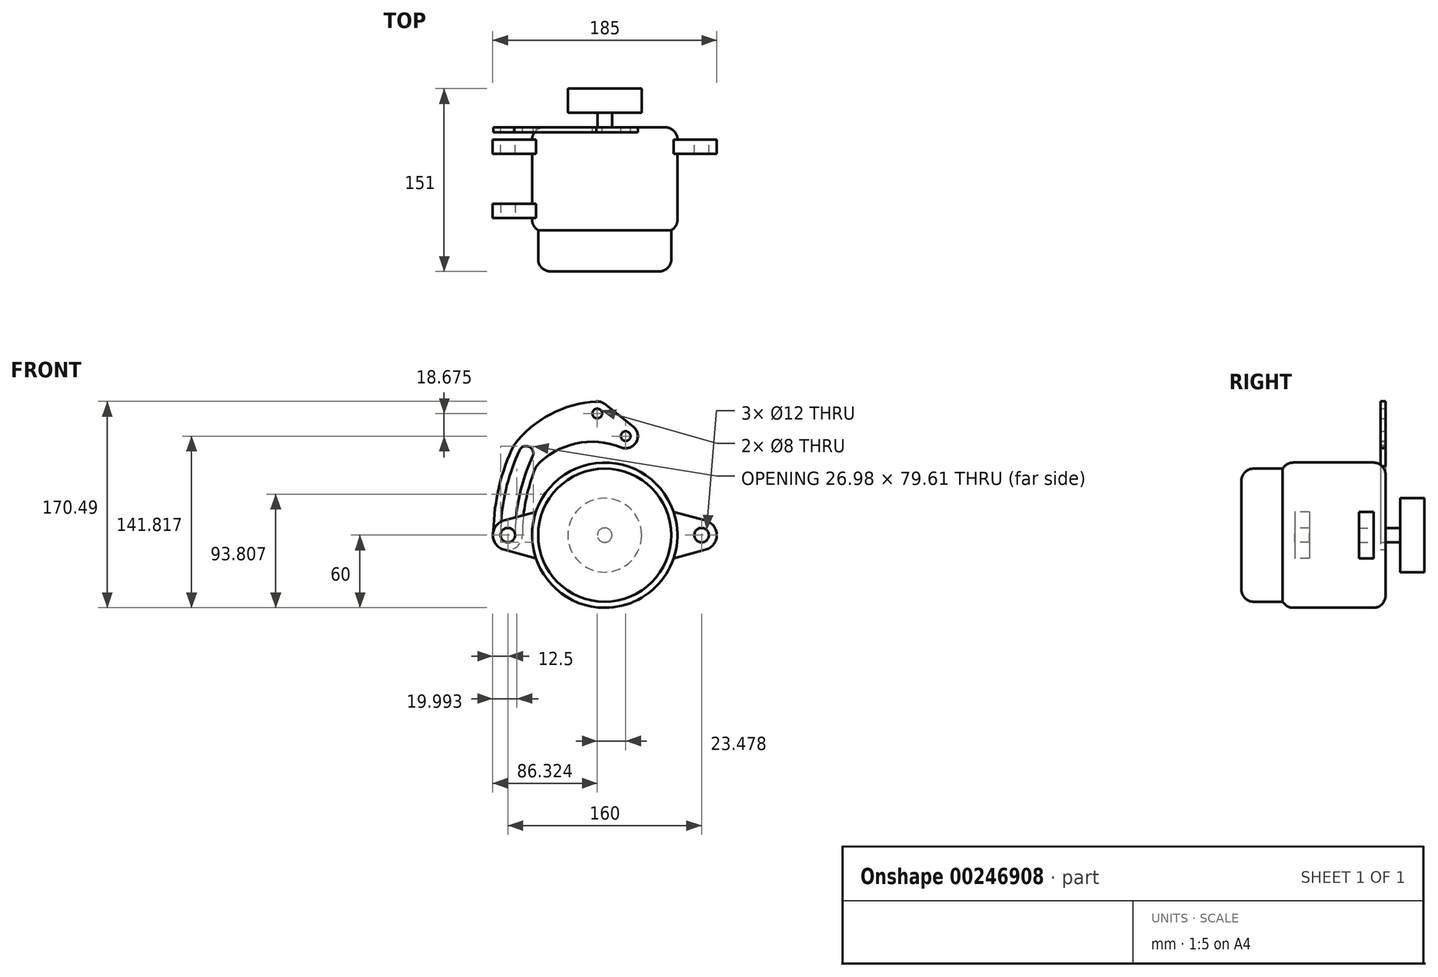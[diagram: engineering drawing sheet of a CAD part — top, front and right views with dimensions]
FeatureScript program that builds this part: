
annotation { "Feature Type Name" : "Feature", "Feature Type Description" : "" }
export const myFeature = defineFeature(function(context is Context, id is Id, definition is map)
    precondition{}
    {
        {
            var Q0;
            Q0=qCreatedBy(makeId("Front.planeOp"),FACE);
            var sketch = newSketch(context, id + "F0", { "sketchPlane" : qUnion([Q0])});
            skCircle(sketch, "E0", {"center": v(0, 0) * mm, "radius": 60 * mm});
            skSolve(sketch);
        }
        {
            var Q0;
            Q0=makeQuery(id+"F0.imprint","IMPRINT",FACE,{"disambiguationData":[TD([[makeQuery(id+"F0.imprint","IMPRINT",EDGE,{"derivedFrom":sQuery(id+"F0.wireOp",EDGE,"E0")}),1.0]])]});
            extrude(context, id + "F1", {"entities" : qUnion([Q0]), "depth" : 85 * mm});
        }
        {
            var Q0;
            Q0=makeQuery(id+"F1.opExtrude","CAP_FACE",FACE,{"disambiguationData":[OSD([sQuery(id+"F0.wireOp",EDGE,"E0")])],"isStart":false});
            var sketch = newSketch(context, id + "F2", { "sketchPlane" : qUnion([Q0])});
            skCircle(sketch, "E1", {"center": v(0, 0) * mm, "radius": 55 * mm});
            skSolve(sketch);
        }
        {
            var Q0;
            Q0 = qSketchRegion(id + "F2", true);
            extrude(context, id + "F3", {"entities" : qUnion([Q0]), "operationType" : NewBodyOperationType.ADD, "depth" : 34 * mm});
        }
        {
            var Q0;
            Q0=makeQuery(id+"F1.opExtrude","CAP_EDGE",EDGE,{"disambiguationData":[OSD([sQuery(id+"F0.wireOp",EDGE,"E0")])],"isStart":true});
            var Q1;
            Q1=makeQuery(id+"F1.opExtrude","CAP_EDGE",EDGE,{"disambiguationData":[OSD([sQuery(id+"F0.wireOp",EDGE,"E0")])],"isStart":false});
            var Q2;
            Q2=makeQuery(id+"F3.opExtrude","CAP_EDGE",EDGE,{"disambiguationData":[OSD([sQuery(id+"F2.wireOp",EDGE,"E1")])],"isStart":false});
            fillet(context, id + "F4", {"entities" : qUnion([Q0, Q1, Q2]), "radius" : 10 * mm, "tangentPropagation" : true, "allowEdgeOverflow" : false});
        }
        {
            var Q0;
            Q0=makeQuery(id+"F1.opExtrude","CAP_FACE",FACE,{"disambiguationData":[OSD([sQuery(id+"F0.wireOp",EDGE,"E0")])],"isStart":true});
            var sketch = newSketch(context, id + "F5", { "sketchPlane" : qUnion([Q0])});
            skCircle(sketch, "E2", {"center": v(0, 0) * mm, "radius": 6 * mm});
            skSolve(sketch);
        }
        {
            var Q0;
            Q0 = qSketchRegion(id + "F5", true);
            extrude(context, id + "F6", {"entities" : qUnion([Q0]), "operationType" : NewBodyOperationType.ADD, "depth" : 12 * mm});
        }
        {
            var Q0;
            Q0=makeQuery(id+"F6.opExtrude","CAP_FACE",FACE,{"disambiguationData":[OSD([sQuery(id+"F5.wireOp",EDGE,"E2")])],"isStart":false});
            var sketch = newSketch(context, id + "F7", { "sketchPlane" : qUnion([Q0])});
            skCircle(sketch, "E3", {"center": v(0, 0) * mm, "radius": 30.5 * mm});
            skSolve(sketch);
        }
        {
            var Q0;
            Q0 = qSketchRegion(id + "F7", true);
            extrude(context, id + "F8", {"entities" : qUnion([Q0]), "operationType" : NewBodyOperationType.ADD, "depth" : 20 * mm});
        }
        {
            var Q0;
            Q0=qCreatedBy(makeId("Front.planeOp"),FACE);
            cPlane(context, id + "F9", {"entities" : qUnion([Q0]), "cplaneType" : CPlaneType.OFFSET, "offset" : 10 * mm, "width" : 150 * mm, "height" : 150 * mm});
        }
        {
            var Q0;
            Q0=qCreatedBy(id+"F9.planeOp",FACE);
            var sketch = newSketch(context, id + "F10", { "sketchPlane" : qUnion([Q0])});
            skCircle(sketch, "E4", {"center": v(-80, 0) * mm, "radius": 6 * mm});
            skCircle(sketch, "E5", {"center": v(80, 0) * mm, "radius": 6 * mm});
            skArc(sketch, "E6", {"start": v(83.24, -12.07) * mm, "mid": v(92.5, 0) * mm, "end": v(83.24, 12.07) * mm});
            skArc(sketch, "E7", {"start": v(-83.24, 12.07) * mm, "mid": v(-92.5, 0) * mm, "end": v(-83.24, -12.07) * mm});
            skLineSegment(sketch, "E8", {"start": v(-83.24, 12.07) * mm, "end": v(-56.87, 19.14) * mm});
            skLineSegment(sketch, "E9", {"start": v(-83.24, -12.07) * mm, "end": v(-56.87, -19.14) * mm});
            skLineSegment(sketch, "E10", {"start": v(83.24, 12.07) * mm, "end": v(56.87, 19.14) * mm});
            skLineSegment(sketch, "E11", {"start": v(83.24, -12.07) * mm, "end": v(56.87, -19.14) * mm});
            skArc(sketch, "E12.0", {"start": v(56.87, -19.14) * mm, "mid": v(60, 0) * mm, "end": v(56.87, 19.14) * mm});
            skArc(sketch, "E13.trimOffspring", {"start": v(-56.87, 19.14) * mm, "mid": v(-60, 0) * mm, "end": v(-56.87, -19.14) * mm});
            skSolve(sketch);
        }
        {
            var Q0;
            Q0 = qSketchRegion(id + "F10", true);
            extrude(context, id + "F11", {"entities" : qUnion([Q0]), "operationType" : NewBodyOperationType.ADD, "depth" : 12 * mm});
        }
        {
            var Q0;
            Q0=qCreatedBy(makeId("Front.planeOp"),FACE);
            cPlane(context, id + "F12", {"entities" : qUnion([Q0]), "cplaneType" : CPlaneType.OFFSET, "offset" : 75 * mm, "width" : 150 * mm, "height" : 150 * mm});
        }
        {
            var Q0;
            Q0=qCreatedBy(id+"F12.planeOp",FACE);
            var sketch = newSketch(context, id + "F13", { "sketchPlane" : qUnion([Q0])});
            skArc(sketch, "E14.0.0", {"start": v(-56.87, -19.14) * mm, "mid": v(-60, 0) * mm, "end": v(-56.87, 19.14) * mm});
            skLineSegment(sketch, "E14.0.1", {"start": v(-56.87, 19.14) * mm, "end": v(-83.24, 12.07) * mm});
            skArc(sketch, "E14.0.2", {"start": v(-83.24, 12.07) * mm, "mid": v(-92.5, 0) * mm, "end": v(-83.24, -12.07) * mm});
            skLineSegment(sketch, "E14.0.3", {"start": v(-83.24, -12.07) * mm, "end": v(-56.87, -19.14) * mm});
            skCircle(sketch, "E15.0", {"center": v(-80, 0) * mm, "radius": 6 * mm});
            skSolve(sketch);
        }
        {
            var Q0;
            Q0 = qSketchRegion(id + "F13", true);
            extrude(context, id + "F14", {"entities" : qUnion([Q0]), "operationType" : NewBodyOperationType.ADD, "oppositeDirection" : true, "depth" : 12 * mm});
        }
        {
            var Q0;
            Q0=qCreatedBy(makeId("Front.planeOp"),FACE);
            var sketch = newSketch(context, id + "F15", { "sketchPlane" : qUnion([Q0])});
            skCircle(sketch, "E16.0", {"center": v(80, 0) * mm, "radius": 6 * mm, "construction": true});
            skArc(sketch, "E17.1", {"start": v(-86, 0) * mm, "mid": v(-80, -6) * mm, "end": v(-74, 0) * mm});
            skArc(sketch, "E18", {"start": v(-62.37, 73) * mm, "mid": v(-76.83, 31.7) * mm, "end": v(-79.55, -12) * mm, "construction": true});
            skArc(sketch, "E19.0", {"start": v(-70.45, 70.15) * mm, "mid": v(-82.07, 35.93) * mm, "end": v(-86, 0) * mm});
            skArc(sketch, "E20.0", {"start": v(-59.57, 65.08) * mm, "mid": v(-70.35, 33.33) * mm, "end": v(-74, 0) * mm});
            skLineSegment(sketch, "E21", {"start": v(80, 0) * mm, "end": v(-80, 0) * mm, "construction": true});
            skLineSegment(sketch, "E22", {"start": v(80, 0) * mm, "end": v(-65, 67.62) * mm, "construction": true});
            skArc(sketch, "E23", {"start": v(-59.57, 65.08) * mm, "mid": v(-62.47, 73.06) * mm, "end": v(-70.45, 70.15) * mm});
            skArc(sketch, "E24.0", {"start": v(-75, 74.58) * mm, "mid": v(-87.7, 38.25) * mm, "end": v(-92, 0) * mm});
            skArc(sketch, "E25.0", {"start": v(-56.6, 56.95) * mm, "mid": v(-65.12, 29.04) * mm, "end": v(-68, 0) * mm});
            skCircle(sketch, "E26", {"center": v(-80, 0) * mm, "radius": 12 * mm});
            skLineSegment(sketch, "E27", {"start": v(-40.68, 127.93) * mm, "end": v(102.08, 14.38) * mm, "construction": true});
            skCircle(sketch, "E28", {"center": v(-6.18, 100.5) * mm, "radius": 4 * mm});
            skCircle(sketch, "E29", {"center": v(17.3, 81.82) * mm, "radius": 4 * mm});
            skArc(sketch, "E30", {"start": v(0.05, 108.32) * mm, "mid": v(-3.2, 110.04) * mm, "end": v(-6.87, 110.47) * mm});
            skArc(sketch, "E31", {"start": v(13.53, 72.55) * mm, "mid": v(25.93, 76.77) * mm, "end": v(23.53, 89.64) * mm});
            skLineSegment(sketch, "E32", {"start": v(0.05, 108.32) * mm, "end": v(23.53, 89.64) * mm});
            skArc(sketch, "E33", {"start": v(13.53, 72.55) * mm, "mid": v(-23.97, 75.7) * mm, "end": v(-56.6, 56.95) * mm});
            skArc(sketch, "E34", {"start": v(-6.87, 110.47) * mm, "mid": v(-44.84, 99.95) * mm, "end": v(-75, 74.58) * mm});
            skLineSegment(sketch, "E35", {"start": v(80, 0) * mm, "end": v(95.56, 19.57) * mm, "construction": true});
            skLineSegment(sketch, "E36", {"start": v(-26.75, -57.7) * mm, "end": v(-116.67, 13.83) * mm, "construction": true});
            skSolve(sketch);
        }
        {
            var Q0;
            Q0 = qSketchRegion(id + "F15", true);
            extrude(context, id + "F16", {"entities" : qUnion([Q0]), "depth" : 4 * mm});
        }
    });
